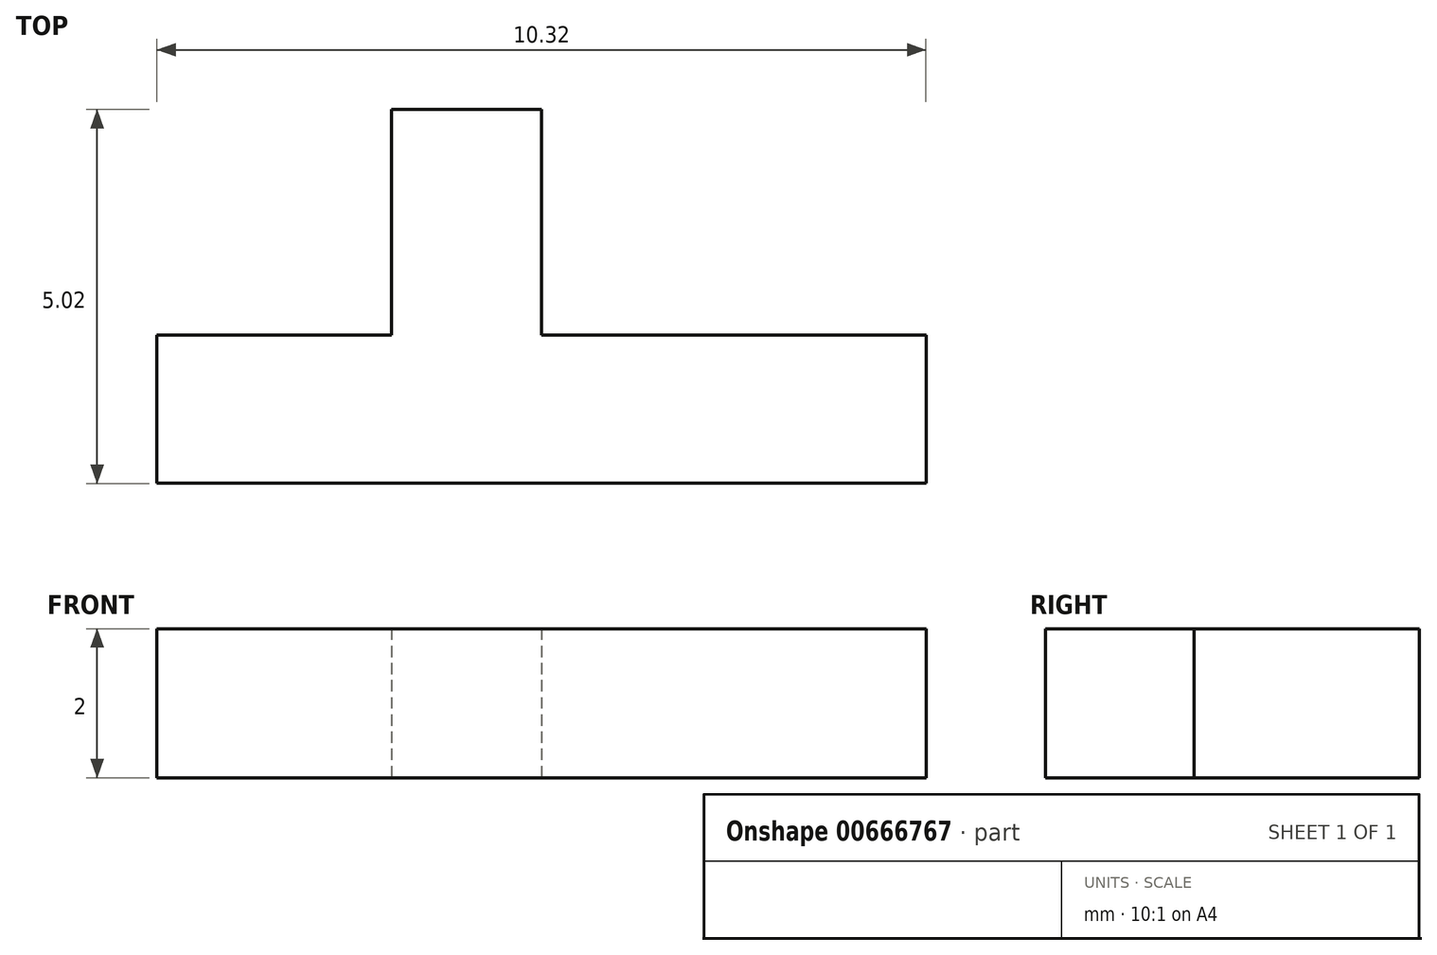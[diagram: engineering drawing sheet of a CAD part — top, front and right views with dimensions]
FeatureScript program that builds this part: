
annotation { "Feature Type Name" : "Feature", "Feature Type Description" : "" }
export const myFeature = defineFeature(function(context is Context, id is Id, definition is map)
    precondition{}
    {
        {
            var Q0;
            Q0=qCreatedBy(makeId("Top.planeOp"),FACE);
            var sketch = newSketch(context, id + "F0", { "sketchPlane" : qUnion([Q0])});
            skLineSegment(sketch, "E0.bottom", {"start": v(5.16, 1) * mm, "end": v(-5.16, 1) * mm});
            skLineSegment(sketch, "E0.top", {"start": v(5.16, -1) * mm, "end": v(-5.16, -1) * mm});
            skLineSegment(sketch, "E0.left", {"start": v(5.16, 1) * mm, "end": v(5.16, -1) * mm});
            skLineSegment(sketch, "E0.right", {"start": v(-5.16, 1) * mm, "end": v(-5.16, -1) * mm});
            skPoint(sketch, "E0.middle", {"position": v(0, 0) * mm});
            skSolve(sketch);
        }
        {
            var Q0;
            Q0 = qSketchRegion(id + "F0", true);
            extrude(context, id + "F1", {"entities" : qUnion([Q0]), "depth" : 2 * mm, "offsetDistance" : 25 * mm});
        }
        {
            var Q0;
            Q0=qCreatedBy(makeId("Top.planeOp"),FACE);
            var sketch = newSketch(context, id + "F2", { "sketchPlane" : qUnion([Q0])});
            skLineSegment(sketch, "E1.bottom", {"start": v(0, 0) * mm, "end": v(-2.01, 0) * mm});
            skLineSegment(sketch, "E1.top", {"start": v(0, 4.02) * mm, "end": v(-2.01, 4.02) * mm});
            skLineSegment(sketch, "E1.left", {"start": v(0, 0) * mm, "end": v(0, 4.02) * mm});
            skLineSegment(sketch, "E1.right", {"start": v(-2.01, 0) * mm, "end": v(-2.01, 4.02) * mm});
            skSolve(sketch);
        }
        {
            var Q0;
            Q0 = qSketchRegion(id + "F2", true);
            extrude(context, id + "F3", {"entities" : qUnion([Q0]), "operationType" : NewBodyOperationType.ADD, "depth" : 2 * mm, "offsetDistance" : 25 * mm});
        }
    });
